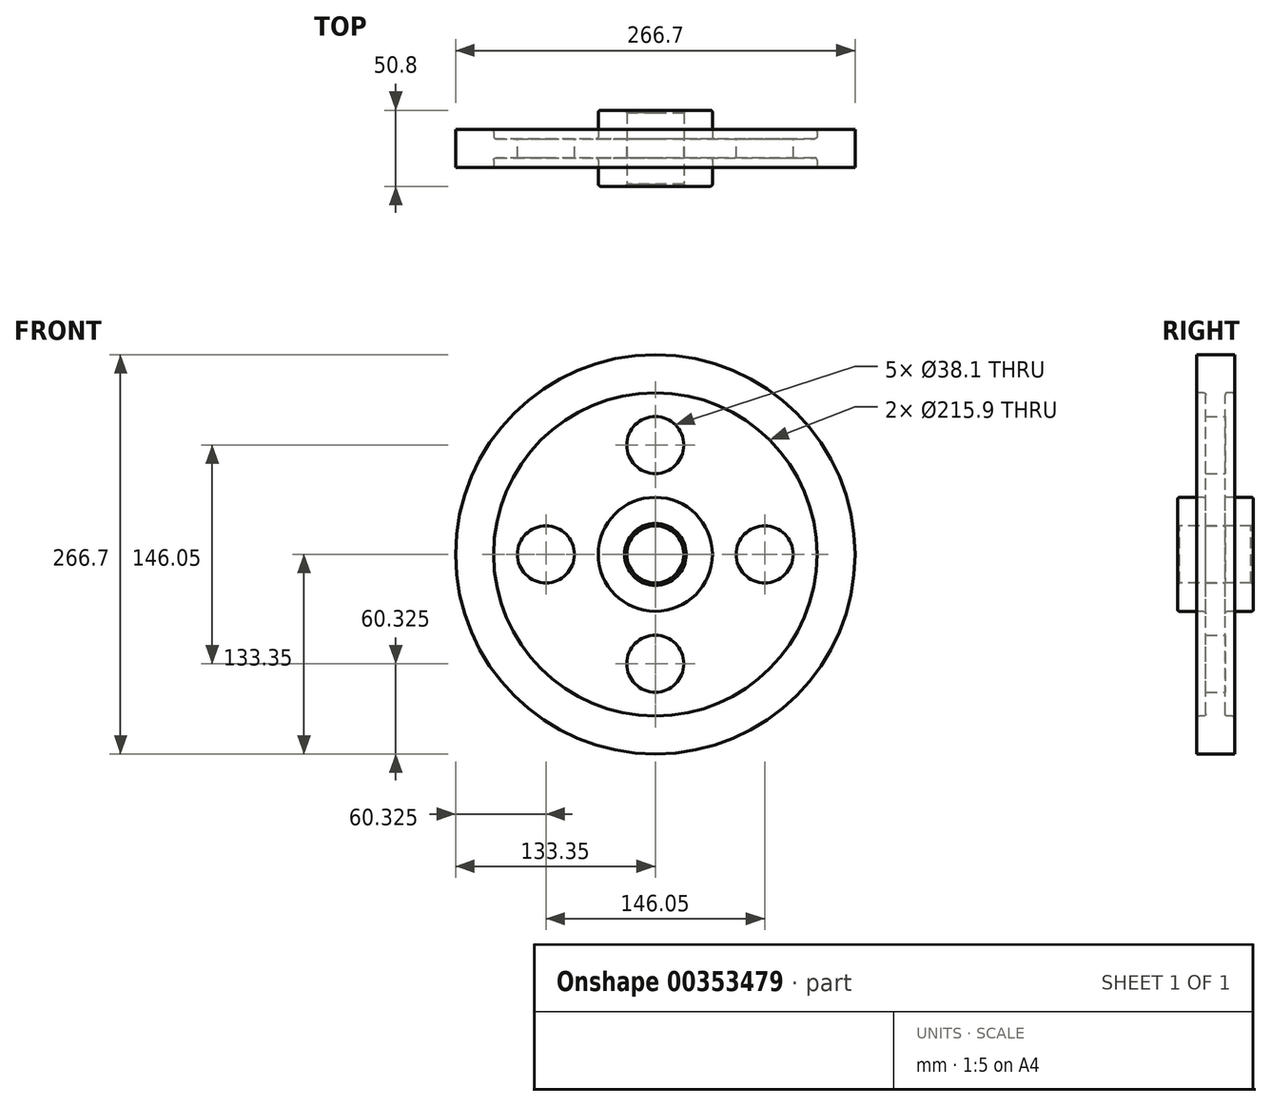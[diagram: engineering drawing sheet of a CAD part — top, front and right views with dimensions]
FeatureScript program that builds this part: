
annotation { "Feature Type Name" : "Feature", "Feature Type Description" : "" }
export const myFeature = defineFeature(function(context is Context, id is Id, definition is map)
    precondition{}
    {
        {
            var Q0;
            Q0=qCreatedBy(makeId("Right.planeOp"),FACE);
            var sketch = newSketch(context, id + "F0", { "sketchPlane" : qUnion([Q0])});
            skLineSegment(sketch, "E0", {"start": v(0, 0) * mm, "end": v(74.75, 0) * mm, "construction": true});
            skLineSegment(sketch, "E1.0", {"start": v(0, 1905) * mm, "end": v(74.75, 1905) * mm});
            skLineSegment(sketch, "E2.0", {"start": v(0, 19.05) * mm, "end": v(25.4, 19.05) * mm});
            skLineSegment(sketch, "E3.0", {"start": v(6.35, 38.1) * mm, "end": v(25.4, 38.1) * mm});
            skLineSegment(sketch, "E4.0", {"start": v(6.35, 107.95) * mm, "end": v(12.7, 107.95) * mm});
            skLineSegment(sketch, "E5.0", {"start": v(0, 133.35) * mm, "end": v(12.7, 133.35) * mm});
            skLineSegment(sketch, "E6", {"start": v(0, 0) * mm, "end": v(0, 133.35) * mm, "construction": true});
            skLineSegment(sketch, "E7.0", {"start": v(25.4, 19.05) * mm, "end": v(25.4, 38.1) * mm});
            skLineSegment(sketch, "E8.trimOffspring", {"start": v(12.7, 107.95) * mm, "end": v(12.7, 133.35) * mm});
            skLineSegment(sketch, "E9.trimOffspring", {"start": v(6.35, 38.1) * mm, "end": v(6.35, 107.95) * mm});
            skLineSegment(sketch, "E10.MirrorCS", {"start": v(-6.35, 38.1) * mm, "end": v(-6.35, 107.95) * mm});
            skLineSegment(sketch, "E11.MirrorCS", {"start": v(-6.35, 107.95) * mm, "end": v(-12.7, 107.95) * mm});
            skLineSegment(sketch, "E12.MirrorCS", {"start": v(-12.7, 107.95) * mm, "end": v(-12.7, 133.35) * mm});
            skLineSegment(sketch, "E13.MirrorCS", {"start": v(-6.35, 38.1) * mm, "end": v(-25.4, 38.1) * mm});
            skLineSegment(sketch, "E14.MirrorCS", {"start": v(-25.4, 19.05) * mm, "end": v(-25.4, 38.1) * mm});
            skLineSegment(sketch, "E15.MirrorCS", {"start": v(0, 19.05) * mm, "end": v(-25.4, 19.05) * mm});
            skLineSegment(sketch, "E16.MirrorCS", {"start": v(0, 133.35) * mm, "end": v(-12.7, 133.35) * mm});
            skSolve(sketch);
        }
        {
            var Q0;
            Q0=makeQuery(id+"F0.imprint","IMPRINT",FACE,{"disambiguationData":[TD([[makeQuery(id+"F0.imprint","IMPRINT",EDGE,{"derivedFrom":sQuery(id+"F0.wireOp",EDGE,"E2.0")}),1.0]])]});
            var Q1;
            Q1=sQuery(id+"F0.wireOp",EDGE,"E0");
            revolve(context, id + "F1", {"entities" : qUnion([Q0]), "axis" : qUnion([Q1]), "revolveType" : RevolveType.FULL});
        }
        {
            var Q0;
            Q0=makeQuery(id+"F1.opRevolve","SWEPT_FACE",FACE,{"disambiguationData":[OSD([sQuery(id+"F0.wireOp",EDGE,"E9.trimOffspring")])]});
            var sketch = newSketch(context, id + "F2", { "sketchPlane" : qUnion([Q0])});
            skLineSegment(sketch, "E17", {"start": v(0, 0) * mm, "end": v(0, 73.03) * mm});
            skCircle(sketch, "E18", {"center": v(0, 73.03) * mm, "radius": 19.05 * mm});
            skCircle(sketch, "E19.1.0", {"center": v(-73.03, 0) * mm, "radius": 19.05 * mm});
            skCircle(sketch, "E19.2.0", {"center": v(0, -73.03) * mm, "radius": 19.05 * mm});
            skCircle(sketch, "E19.3.0", {"center": v(73.03, 0) * mm, "radius": 19.05 * mm});
            skPoint(sketch, "E19.center", {"position": v(0, 0) * mm});
            skSolve(sketch);
        }
        {
            var Q0;
            Q0=makeQuery(id+"F2.imprint","IMPRINT",FACE,{"disambiguationData":[TD([[makeQuery(id+"F2.imprint","IMPRINT",EDGE,{"derivedFrom":sQuery(id+"F2.wireOp",EDGE,"E19.2.0")}),1.0]])]});
            var Q1;
            Q1=makeQuery(id+"F2.imprint","IMPRINT",FACE,{"disambiguationData":[TD([[makeQuery(id+"F2.imprint","IMPRINT",EDGE,{"derivedFrom":sQuery(id+"F2.wireOp",EDGE,"E19.1.0")}),1.0]])]});
            var Q2;
            Q2=makeQuery(id+"F2.imprint","IMPRINT",FACE,{"disambiguationData":[TD([[makeQuery(id+"F2.imprint","IMPRINT",EDGE,{"derivedFrom":sQuery(id+"F2.wireOp",EDGE,"E18")}),1.0]])]});
            var Q3;
            Q3=makeQuery(id+"F2.imprint","IMPRINT",FACE,{"disambiguationData":[TD([[makeQuery(id+"F2.imprint","IMPRINT",EDGE,{"derivedFrom":sQuery(id+"F2.wireOp",EDGE,"E19.3.0")}),1.0]])]});
            extrude(context, id + "F3", {"entities" : qUnion([Q0, Q1, Q2, Q3]), "operationType" : NewBodyOperationType.REMOVE, "oppositeDirection" : true, "depth" : 25.4 * mm});
        }
        {
            var Q0;
            Q0=makeQuery(id+"F1.opRevolve","SWEPT_EDGE",EDGE,{"disambiguationData":[OSD([sQuery(id+"F0.wireOp",EDGE,"E10.MirrorCS"),sQuery(id+"F0.wireOp",EDGE,"E13.MirrorCS")])]});
            var Q1;
            Q1=makeQuery(id+"F1.opRevolve","SWEPT_EDGE",EDGE,{"disambiguationData":[OSD([sQuery(id+"F0.wireOp",EDGE,"E13.MirrorCS"),sQuery(id+"F0.wireOp",EDGE,"E14.MirrorCS")])]});
            var Q2;
            Q2=makeQuery(id+"F1.opRevolve","SWEPT_EDGE",EDGE,{"disambiguationData":[OSD([sQuery(id+"F0.wireOp",EDGE,"E10.MirrorCS"),sQuery(id+"F0.wireOp",EDGE,"E11.MirrorCS")])]});
            var Q3;
            Q3=makeQuery(id+"F1.opRevolve","SWEPT_EDGE",EDGE,{"disambiguationData":[OSD([sQuery(id+"F0.wireOp",EDGE,"E11.MirrorCS"),sQuery(id+"F0.wireOp",EDGE,"E12.MirrorCS")])]});
            var Q4;
            Q4=makeQuery(id+"F1.opRevolve","SWEPT_EDGE",EDGE,{"disambiguationData":[OSD([sQuery(id+"F0.wireOp",EDGE,"E3.0"),sQuery(id+"F0.wireOp",EDGE,"E9.trimOffspring")])]});
            var Q5;
            Q5=makeQuery(id+"F1.opRevolve","SWEPT_EDGE",EDGE,{"disambiguationData":[OSD([sQuery(id+"F0.wireOp",EDGE,"E3.0"),sQuery(id+"F0.wireOp",EDGE,"E7.0")])]});
            var Q6;
            Q6=makeQuery(id+"F1.opRevolve","SWEPT_EDGE",EDGE,{"disambiguationData":[OSD([sQuery(id+"F0.wireOp",EDGE,"E4.0"),sQuery(id+"F0.wireOp",EDGE,"E9.trimOffspring")])]});
            var Q7;
            Q7=makeQuery(id+"F1.opRevolve","SWEPT_EDGE",EDGE,{"disambiguationData":[OSD([sQuery(id+"F0.wireOp",EDGE,"E4.0"),sQuery(id+"F0.wireOp",EDGE,"E8.trimOffspring")])]});
            fillet(context, id + "F4", {"entities" : qUnion([Q0, Q1, Q2, Q3, Q4, Q5, Q6, Q7]), "radius" : 1.59 * mm, "tangentPropagation" : true, "allowEdgeOverflow" : false});
        }
        {
            var Q0;
            Q0=makeQuery(id+"F1.opRevolve","SWEPT_EDGE",EDGE,{"disambiguationData":[OSD([sQuery(id+"F0.wireOp",EDGE,"E14.MirrorCS"),sQuery(id+"F0.wireOp",EDGE,"E15.MirrorCS")])]});
            var Q1;
            Q1=makeQuery(id+"F1.opRevolve","SWEPT_EDGE",EDGE,{"disambiguationData":[OSD([sQuery(id+"F0.wireOp",EDGE,"E2.0"),sQuery(id+"F0.wireOp",EDGE,"E7.0")])]});
            chamfer(context, id + "F5", {"entities" : qUnion([Q0, Q1]), "width" : 1.59 * mm, "tangentPropagation" : true});
        }
    });
